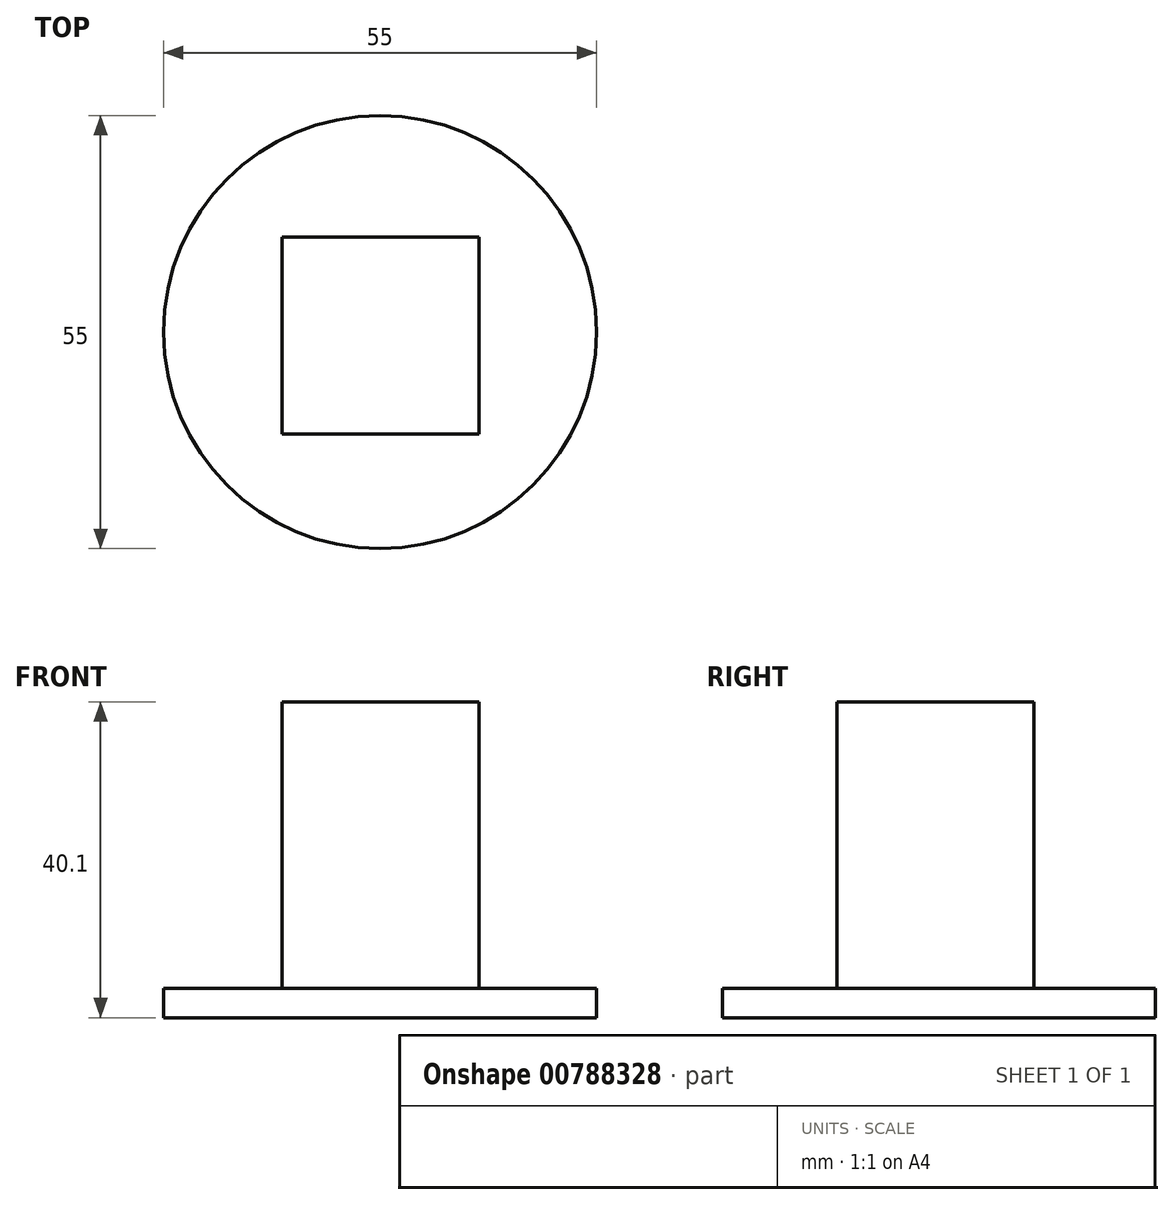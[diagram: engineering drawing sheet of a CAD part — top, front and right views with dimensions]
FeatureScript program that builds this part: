
annotation { "Feature Type Name" : "Feature", "Feature Type Description" : "" }
export const myFeature = defineFeature(function(context is Context, id is Id, definition is map)
    precondition{}
    {
        {
            var Q0;
            Q0=qCreatedBy(makeId("Top.planeOp"),FACE);
            var sketch = newSketch(context, id + "F0", { "sketchPlane" : qUnion([Q0])});
            skCircle(sketch, "E0", {"center": v(0, 0) * mm, "radius": 27.5 * mm});
            skSolve(sketch);
        }
        {
            var Q0;
            Q0=qCreatedBy(makeId("Top.planeOp"),FACE);
            var sketch = newSketch(context, id + "F1", { "sketchPlane" : qUnion([Q0])});
            skLineSegment(sketch, "E1.bottom", {"start": v(-12.44, 12.03) * mm, "end": v(12.56, 12.03) * mm});
            skLineSegment(sketch, "E1.top", {"start": v(-12.44, -12.97) * mm, "end": v(12.56, -12.97) * mm});
            skLineSegment(sketch, "E1.left", {"start": v(-12.44, 12.03) * mm, "end": v(-12.44, -12.97) * mm});
            skLineSegment(sketch, "E1.right", {"start": v(12.56, 12.03) * mm, "end": v(12.56, -12.97) * mm});
            skSolve(sketch);
        }
        {
            var Q0;
            Q0 = qSketchRegion(id + "F1", true);
            extrude(context, id + "F2", {"entities" : qUnion([Q0]), "depth" : 40.1 * mm, "offsetDistance" : 25 * mm});
        }
        {
            var Q0;
            Q0 = qSketchRegion(id + "F0", true);
            extrude(context, id + "F3", {"entities" : qUnion([Q0]), "operationType" : NewBodyOperationType.ADD, "depth" : 3.7 * mm, "offsetDistance" : 25 * mm});
        }
    });
